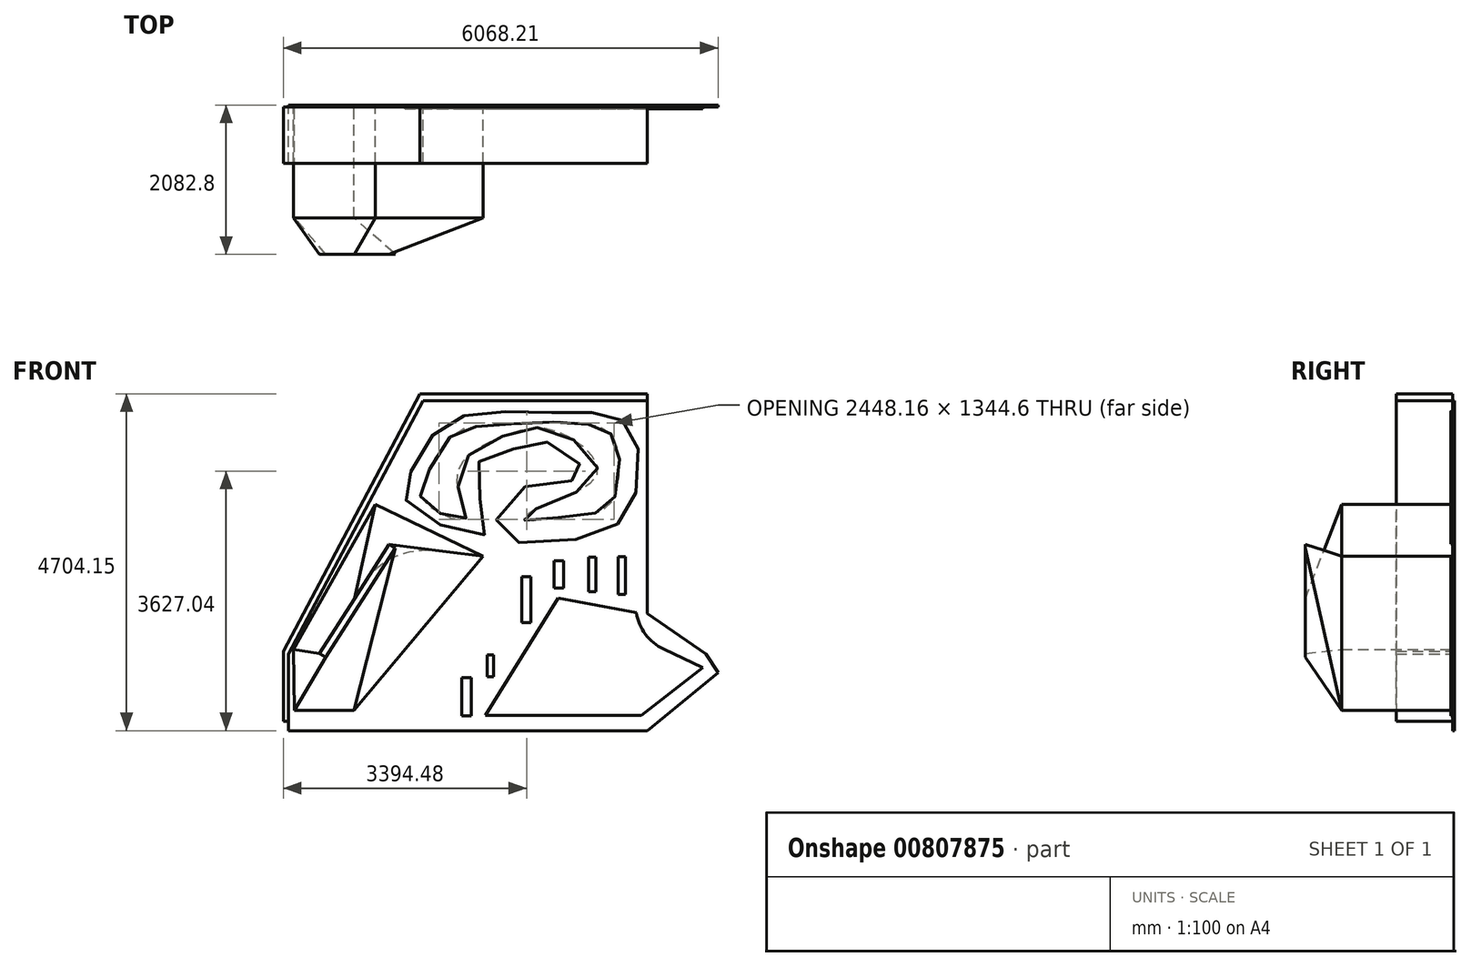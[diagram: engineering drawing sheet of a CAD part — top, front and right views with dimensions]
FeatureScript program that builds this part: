
annotation { "Feature Type Name" : "Feature", "Feature Type Description" : "" }
export const myFeature = defineFeature(function(context is Context, id is Id, definition is map)
    precondition{}
    {
        {
            var Q0;
            Q0=qCreatedBy(makeId("Front.planeOp"),FACE);
            var sketch = newSketch(context, id + "F0", { "sketchPlane" : qUnion([Q0])});
            skLineSegment(sketch, "E0.bottom", {"start": v(0, 0) * mm, "end": v(3810, 0) * mm});
            skLineSegment(sketch, "E0.top", {"start": v(1905, 4572) * mm, "end": v(3810, 4572) * mm});
            skLineSegment(sketch, "E0.left", {"start": v(0, 0) * mm, "end": v(0, 977.16) * mm});
            skLineSegment(sketch, "E1", {"start": v(1905, 4572) * mm, "end": v(0, 977.16) * mm});
            skPoint(sketch, "E2.orphan", {"position": v(0, 4572) * mm});
            skLineSegment(sketch, "E3", {"start": v(3810, 4572) * mm, "end": v(5080, 4572) * mm});
            skLineSegment(sketch, "E4", {"start": v(3810, 0) * mm, "end": v(5080, 0) * mm});
            skLineSegment(sketch, "E5", {"start": v(5080, 4572) * mm, "end": v(5080, 1518.6) * mm});
            skArc(sketch, "E6", {"start": v(5080, 1518.6) * mm, "mid": v(5146.41, 1287.08) * mm, "end": v(5325.45, 1125.96) * mm});
            skLineSegment(sketch, "E7", {"start": v(5325.45, 1125.96) * mm, "end": v(6071.5, 762.42) * mm});
            skLineSegment(sketch, "E8", {"start": v(6071.5, 762.42) * mm, "end": v(5080, 0) * mm});
            skPoint(sketch, "E9.end.orphan", {"position": v(3908.05, 0) * mm});
            skLineSegment(sketch, "E10", {"start": v(141.92, 1005.14) * mm, "end": v(153.82, 153.5) * mm});
            skLineSegment(sketch, "E11", {"start": v(153.82, 153.5) * mm, "end": v(985.88, 153.09) * mm});
            skLineSegment(sketch, "E12", {"start": v(985.88, 153.09) * mm, "end": v(2786.7, 2305.94) * mm});
            skLineSegment(sketch, "E13", {"start": v(2786.7, 2305.94) * mm, "end": v(1283.18, 3028.72) * mm});
            skLineSegment(sketch, "E14", {"start": v(1283.18, 3028.72) * mm, "end": v(141.92, 1005.14) * mm});
            skLineSegment(sketch, "E15", {"start": v(0, 977.16) * mm, "end": v(71.79, 939.12) * mm});
            skLineSegment(sketch, "E16", {"start": v(71.79, 939.12) * mm, "end": v(71.79, 0) * mm});
            skLineSegment(sketch, "E17", {"start": v(71.79, 0) * mm, "end": v(71.79, 939.12) * mm});
            skLineSegment(sketch, "E18", {"start": v(71.79, 939.12) * mm, "end": v(1996.95, 4572) * mm});
            skLineSegment(sketch, "E19", {"start": v(1905, 4572) * mm, "end": v(1947.78, 4479.21) * mm});
            skLineSegment(sketch, "E20", {"start": v(1947.78, 4479.21) * mm, "end": v(5080, 4479.21) * mm});
            skFitSpline(sketch, "E21", {"points": [v(1708.58, 3275.36) * mm, v(2109.58, 4028.05) * mm, v(2793.87, 4311.58) * mm, v(3872.47, 4311.04) * mm, v(4575.1, 4273.65) * mm, v(4920.08, 3946.4) * mm, v(4864.14, 3020.75) * mm, v(4296.89, 2589.05) * mm, v(3008.74, 2626.73) * mm, v(3372.71, 3274.52) * mm, v(4192.53, 3422.22) * mm, v(3779.8, 3872.93) * mm, v(3163.41, 3786.84) * mm, v(2657.86, 3490.87) * mm, v(2830, 2626.82) * mm, v(1825.53, 2960.57) * mm, v(1708.58, 3275.36) * mm]});
            skLineSegment(sketch, "E22", {"start": v(3372.71, 3274.52) * mm, "end": v(3526.64, 2965.88) * mm});
            skFitSpline(sketch, "E23", {"points": [v(3526.64, 2965.88) * mm, v(3347.83, 2817.87) * mm, v(4099.8, 2879.2) * mm, v(4586.8, 3045.58) * mm, v(4667.32, 3823.1) * mm, v(4476.38, 4082.4) * mm, v(3866.25, 4181.44) * mm, v(2830.76, 4126.42) * mm, v(2331.44, 3972.4) * mm, v(1930.45, 3244.4) * mm, v(1973.5, 3046.9) * mm, v(2528.09, 2812.1) * mm, v(2423.62, 3429.28) * mm, v(3027.9, 3965.87) * mm, v(3816.87, 4051.87) * mm, v(4383.61, 3459.15) * mm, v(3526.64, 2965.88) * mm]});
            skSolve(sketch);
        }
        {
            var Q0;
            {var subQ0=sQuery(id+"F0.wireOp",EDGE,"E4");Q0=makeQuery(id+"F0.imprint","IMPRINT",FACE,{"disambiguationData":[TD([[makeQuery(id+"F0.imprint","IMPRINT",EDGE,{"derivedFrom":subQ0}),1.0]])]});}
            var sketch = newSketch(context, id + "F1", { "sketchPlane" : qUnion([Q0])});
            skLineSegment(sketch, "E24", {"start": v(3837.36, 1720) * mm, "end": v(2819.86, 84.35) * mm});
            skLineSegment(sketch, "E25", {"start": v(2819.86, 84.35) * mm, "end": v(4997.1, 84.35) * mm});
            skLineSegment(sketch, "E26", {"start": v(4997.1, 84.35) * mm, "end": v(5855.95, 751.74) * mm});
            skLineSegment(sketch, "E27", {"start": v(5855.95, 751.74) * mm, "end": v(5308.9, 1008.85) * mm});
            skArc(sketch, "E28", {"start": v(4925.97, 1517.6) * mm, "mid": v(5054.35, 1215.74) * mm, "end": v(5308.9, 1008.85) * mm});
            skLineSegment(sketch, "E29", {"start": v(4925.97, 1517.6) * mm, "end": v(3837.36, 1720) * mm});
            skLineSegment(sketch, "E30.bottom", {"start": v(1605.43, 494.63) * mm, "end": v(1485.08, 494.63) * mm});
            skLineSegment(sketch, "E30.top", {"start": v(1605.43, 95.3) * mm, "end": v(1485.08, 95.3) * mm});
            skLineSegment(sketch, "E30.left", {"start": v(1605.43, 494.63) * mm, "end": v(1605.43, 95.3) * mm});
            skLineSegment(sketch, "E30.right", {"start": v(1485.08, 494.63) * mm, "end": v(1485.08, 95.3) * mm});
            skLineSegment(sketch, "E31.bottom", {"start": v(1846.13, 921.32) * mm, "end": v(1906.3, 921.32) * mm});
            skLineSegment(sketch, "E31.top", {"start": v(1846.13, 560.28) * mm, "end": v(1906.3, 560.28) * mm});
            skLineSegment(sketch, "E31.left", {"start": v(1846.13, 921.32) * mm, "end": v(1846.13, 560.28) * mm});
            skLineSegment(sketch, "E31.right", {"start": v(1906.3, 921.32) * mm, "end": v(1906.3, 560.28) * mm});
            skLineSegment(sketch, "E32.bottom", {"start": v(2907.4, 2037.29) * mm, "end": v(2989.45, 2037.29) * mm});
            skLineSegment(sketch, "E32.top", {"start": v(2907.4, 1659.83) * mm, "end": v(2989.45, 1659.83) * mm});
            skLineSegment(sketch, "E32.left", {"start": v(2907.4, 2037.29) * mm, "end": v(2907.4, 1659.83) * mm});
            skLineSegment(sketch, "E32.right", {"start": v(2989.45, 2037.29) * mm, "end": v(2989.45, 1659.83) * mm});
            skLineSegment(sketch, "E33.bottom", {"start": v(4674.34, 2299.87) * mm, "end": v(4778.27, 2299.87) * mm});
            skLineSegment(sketch, "E33.top", {"start": v(4674.34, 1769.24) * mm, "end": v(4778.27, 1769.24) * mm});
            skLineSegment(sketch, "E33.left", {"start": v(4674.34, 2299.87) * mm, "end": v(4674.34, 1769.24) * mm});
            skLineSegment(sketch, "E33.right", {"start": v(4778.27, 2299.87) * mm, "end": v(4778.27, 1769.24) * mm});
            skLineSegment(sketch, "E34.bottom", {"start": v(3328.61, 2020.88) * mm, "end": v(3454.43, 2020.88) * mm});
            skLineSegment(sketch, "E34.top", {"start": v(3328.61, 1375.37) * mm, "end": v(3454.43, 1375.37) * mm});
            skLineSegment(sketch, "E34.left", {"start": v(3328.61, 2020.88) * mm, "end": v(3328.61, 1375.37) * mm});
            skLineSegment(sketch, "E34.right", {"start": v(3454.43, 2020.88) * mm, "end": v(3454.43, 1375.37) * mm});
            skLineSegment(sketch, "E35.bottom", {"start": v(2486.17, 609.51) * mm, "end": v(2622.93, 609.51) * mm});
            skLineSegment(sketch, "E35.top", {"start": v(2486.17, 73.4) * mm, "end": v(2622.93, 73.4) * mm});
            skLineSegment(sketch, "E35.left", {"start": v(2486.17, 609.51) * mm, "end": v(2486.17, 73.4) * mm});
            skLineSegment(sketch, "E35.right", {"start": v(2622.93, 609.51) * mm, "end": v(2622.93, 73.4) * mm});
            skLineSegment(sketch, "E36.bottom", {"start": v(2847.22, 926.8) * mm, "end": v(2934.74, 926.8) * mm});
            skLineSegment(sketch, "E36.top", {"start": v(2847.22, 620.45) * mm, "end": v(2934.74, 620.45) * mm});
            skLineSegment(sketch, "E36.left", {"start": v(2847.22, 926.8) * mm, "end": v(2847.22, 620.45) * mm});
            skLineSegment(sketch, "E36.right", {"start": v(2934.74, 926.8) * mm, "end": v(2934.74, 620.45) * mm});
            skLineSegment(sketch, "E37.bottom", {"start": v(4264.05, 2294.4) * mm, "end": v(4362.52, 2294.4) * mm});
            skLineSegment(sketch, "E37.top", {"start": v(4264.05, 1813) * mm, "end": v(4362.52, 1813) * mm});
            skLineSegment(sketch, "E37.left", {"start": v(4264.05, 2294.4) * mm, "end": v(4264.05, 1813) * mm});
            skLineSegment(sketch, "E37.right", {"start": v(4362.52, 2294.4) * mm, "end": v(4362.52, 1813) * mm});
            skLineSegment(sketch, "E38.bottom", {"start": v(3777.19, 2239.7) * mm, "end": v(3913.95, 2239.7) * mm});
            skLineSegment(sketch, "E38.top", {"start": v(3777.19, 1862.24) * mm, "end": v(3913.95, 1862.24) * mm});
            skLineSegment(sketch, "E38.left", {"start": v(3777.19, 2239.7) * mm, "end": v(3777.19, 1862.24) * mm});
            skLineSegment(sketch, "E38.right", {"start": v(3913.95, 2239.7) * mm, "end": v(3913.95, 1862.24) * mm});
            skLineSegment(sketch, "E39.bottom", {"start": v(2201.7, 697.04) * mm, "end": v(2141.53, 697.04) * mm});
            skLineSegment(sketch, "E39.top", {"start": v(2201.7, 259.4) * mm, "end": v(2141.53, 259.4) * mm});
            skLineSegment(sketch, "E39.left", {"start": v(2201.7, 697.04) * mm, "end": v(2201.7, 259.4) * mm});
            skLineSegment(sketch, "E39.right", {"start": v(2141.53, 697.04) * mm, "end": v(2141.53, 259.4) * mm});
            skLineSegment(sketch, "E40", {"start": v(2070.42, 1462.9) * mm, "end": v(3273.2, 813.1) * mm});
            skLineSegment(sketch, "E41", {"start": v(2163.41, 1555.9) * mm, "end": v(3328.61, 902.18) * mm});
            skLineSegment(sketch, "E42", {"start": v(3328.61, 902.18) * mm, "end": v(2163.41, 1555.9) * mm});
            skLineSegment(sketch, "E43", {"start": v(2070.42, 1462.9) * mm, "end": v(2163.41, 1555.9) * mm});
            skSolve(sketch);
        }
        {
            var Q0;
            Q0=makeQuery(id+"F0.imprint","IMPRINT",FACE,{"disambiguationData":[TD([[makeQuery(id+"F0.imprint","IMPRINT",EDGE,{"derivedFrom":sQuery(id+"F0.wireOp",EDGE,"E21")}),-1.0]])]});
            var Q1;
            Q1=makeQuery(id+"F0.imprint","IMPRINT",FACE,{"disambiguationData":[TD([[makeQuery(id+"F0.imprint","IMPRINT",EDGE,{"derivedFrom":sQuery(id+"F0.wireOp",EDGE,"E10")}),1.0]])]});
            var Q2;
            {var subQ0=sQuery(id+"F1.wireOp",EDGE,"E25");Q2=makeQuery(id+"F1.imprint","IMPRINT",FACE,{"disambiguationData":[TD([[makeQuery(id+"F1.imprint","IMPRINT",EDGE,{"derivedFrom":subQ0}),1.0]])]});}
            var Q3;
            Q3=makeQuery(id+"F0.imprint","IMPRINT",FACE,{"disambiguationData":[TD([[makeQuery(id+"F0.imprint","IMPRINT",EDGE,{"derivedFrom":sQuery(id+"F0.wireOp",EDGE,"E1")}),1.0]])]});
            var Q4;
            {var subQ0=sQuery(id+"F0.wireOp",EDGE,"E19");Q4=makeQuery(id+"F0.imprint","IMPRINT",FACE,{"disambiguationData":[TD([[makeQuery(id+"F0.imprint","IMPRINT",EDGE,{"derivedFrom":subQ0}),1.0]])]});}
            var Q5;
            {var subQ4=sQuery(id+"F0.wireOp",EDGE,"E3");Q5=makeQuery(id+"F0.imprint","IMPRINT",FACE,{"disambiguationData":[TD([[makeQuery(id+"F0.imprint","IMPRINT",EDGE,{"derivedFrom":subQ4}),-1.0]])]});}
            var Q6;
            {var subQ0=sQuery(id+"F0.wireOp",EDGE,"E0.left");Q6=makeQuery(id+"F0.imprint","IMPRINT",FACE,{"disambiguationData":[TD([[makeQuery(id+"F0.imprint","IMPRINT",EDGE,{"derivedFrom":subQ0}),-1.0]])]});}
            var Q7;
            Q7=makeQuery(id+"F1.imprint","IMPRINT",FACE,{"disambiguationData":[TD([[makeQuery(id+"F1.imprint","IMPRINT",EDGE,{"derivedFrom":sQuery(id+"F1.wireOp",EDGE,"E35.bottom")}),-1.0]])]});
            var Q8;
            Q8=makeQuery(id+"F1.imprint","IMPRINT",FACE,{"disambiguationData":[TD([[makeQuery(id+"F1.imprint","IMPRINT",EDGE,{"derivedFrom":sQuery(id+"F1.wireOp",EDGE,"E36.bottom")}),-1.0]])]});
            var Q9;
            Q9=makeQuery(id+"F1.imprint","IMPRINT",FACE,{"disambiguationData":[TD([[makeQuery(id+"F1.imprint","IMPRINT",EDGE,{"derivedFrom":sQuery(id+"F1.wireOp",EDGE,"E34.bottom")}),-1.0]])]});
            var Q10;
            Q10=makeQuery(id+"F1.imprint","IMPRINT",FACE,{"disambiguationData":[TD([[makeQuery(id+"F1.imprint","IMPRINT",EDGE,{"derivedFrom":sQuery(id+"F1.wireOp",EDGE,"E38.bottom")}),-1.0]])]});
            var Q11;
            Q11=makeQuery(id+"F1.imprint","IMPRINT",FACE,{"disambiguationData":[TD([[makeQuery(id+"F1.imprint","IMPRINT",EDGE,{"derivedFrom":sQuery(id+"F1.wireOp",EDGE,"E37.bottom")}),-1.0]])]});
            var Q12;
            Q12=makeQuery(id+"F1.imprint","IMPRINT",FACE,{"disambiguationData":[TD([[makeQuery(id+"F1.imprint","IMPRINT",EDGE,{"derivedFrom":sQuery(id+"F1.wireOp",EDGE,"E33.bottom")}),-1.0]])]});
            extrude(context, id + "F2", {"entities" : qUnion([Q0, Q1, Q2, Q3, Q4, Q5, Q6, Q7, Q8, Q9, Q10, Q11, Q12]), "depth" : 25.4 * mm, "offsetDistance" : 25.4 * mm});
        }
        {
            var Q0;
            Q0=makeQuery(id+"F2.opExtrude","CAP_FACE",FACE,{"disambiguationData":[OSD([sQuery(id+"F0.wireOp",EDGE,"E10"),sQuery(id+"F0.wireOp",EDGE,"E11"),sQuery(id+"F0.wireOp",EDGE,"E12"),sQuery(id+"F0.wireOp",EDGE,"E13"),sQuery(id+"F0.wireOp",EDGE,"E14")])],"isStart":false});
            var sketch = newSketch(context, id + "F3", { "sketchPlane" : qUnion([Q0])});
            skSolve(sketch);
        }
        {
            var Q0;
            Q0=makeQuery(id+"F3.imprint","IMPRINT",FACE,{"disambiguationData":[TD([[makeQuery(id+"F3.imprint","IMPRINT",EDGE,{"derivedFrom":makeQuery(id+"F2.opExtrude","CAP_EDGE",EDGE,{"disambiguationData":[OSD([sQuery(id+"F0.wireOp",EDGE,"E10")])],"isStart":false})}),1.0]])]});
            extrude(context, id + "F4", {"entities" : qUnion([Q0]), "operationType" : NewBodyOperationType.ADD, "depth" : 1524 * mm, "offsetDistance" : 25.4 * mm});
        }
        {
            var Q0;
            Q0=makeQuery(id+"F4.opExtrude","CAP_FACE",FACE,{"disambiguationData":[OSD([sQuery(id+"F0.wireOp",EDGE,"E10"),sQuery(id+"F0.wireOp",EDGE,"E11"),sQuery(id+"F0.wireOp",EDGE,"E12"),sQuery(id+"F0.wireOp",EDGE,"E13"),sQuery(id+"F0.wireOp",EDGE,"E14")])],"isStart":false});
            cPlane(context, id + "F5", {"entities" : qUnion([Q0]), "cplaneType" : CPlaneType.OFFSET, "offset" : 508 * mm, "width" : 152.4 * mm, "height" : 152.4 * mm});
        }
        {
            var Q0;
            Q0=qCreatedBy(id+"F5.planeOp",FACE);
            var sketch = newSketch(context, id + "F6", { "sketchPlane" : qUnion([Q0])});
            skLineSegment(sketch, "E44", {"start": v(503.02, 944.77) * mm, "end": v(1474.87, 2472.2) * mm});
            skLineSegment(sketch, "E45", {"start": v(1474.87, 2472.2) * mm, "end": v(1560.92, 2417.45) * mm});
            skLineSegment(sketch, "E46", {"start": v(1560.92, 2417.45) * mm, "end": v(593.25, 896.58) * mm});
            skLineSegment(sketch, "E47", {"start": v(593.25, 896.58) * mm, "end": v(503.02, 944.77) * mm});
            skSolve(sketch);
        }
        {
            var Q1;
            Q1=makeQuery(id+"F6.imprint","IMPRINT",FACE,{"disambiguationData":[TD([[makeQuery(id+"F6.imprint","IMPRINT",EDGE,{"derivedFrom":sQuery(id+"F6.wireOp",EDGE,"E44")}),-1.0]])]});
            var Q2;
            Q2=makeQuery(id+"F4.opExtrude","CAP_FACE",FACE,{"disambiguationData":[OSD([sQuery(id+"F0.wireOp",EDGE,"E10"),sQuery(id+"F0.wireOp",EDGE,"E11"),sQuery(id+"F0.wireOp",EDGE,"E12"),sQuery(id+"F0.wireOp",EDGE,"E13"),sQuery(id+"F0.wireOp",EDGE,"E14")])],"isStart":false});
            loft(context, id + "F7", {"operationType" : NewBodyOperationType.ADD, "sheetProfilesArray" : [{ "sheetProfileEntities" : qUnion([Q1]) }, { "sheetProfileEntities" : qUnion([Q2]) }]});
        }
        {
            var Q0;
            Q0=makeQuery(id+"F2.opExtrude","CAP_FACE",FACE,{"disambiguationData":[OSD([sQuery(id+"F0.wireOp",EDGE,"E0.bottom"),sQuery(id+"F0.wireOp",EDGE,"E0.top"),sQuery(id+"F0.wireOp",EDGE,"E0.left"),sQuery(id+"F0.wireOp",EDGE,"E1"),sQuery(id+"F0.wireOp",EDGE,"E3"),sQuery(id+"F0.wireOp",EDGE,"E5"),sQuery(id+"F0.wireOp",EDGE,"E17"),sQuery(id+"F0.wireOp",EDGE,"E18"),sQuery(id+"F0.wireOp",EDGE,"E20")])],"isStart":false});
            extrude(context, id + "F8", {"entities" : qUnion([Q0]), "operationType" : NewBodyOperationType.ADD, "depth" : 762 * mm, "offsetDistance" : 25.4 * mm});
        }
        {
            var Q0;
            {var subQ0=sQuery(id+"F0.wireOp",EDGE,"E5");Q0=makeQuery(id+"F8.boolean.opBoolean","MERGE",FACE,{"derivedFrom":[makeQuery(id+"F2.opExtrude","SWEPT_FACE",FACE,{"disambiguationData":[OSD([subQ0])]}),makeQuery(id+"F8.opExtrude","SWEPT_FACE",FACE,{"disambiguationData":[OSD([subQ0])]})]});}
            var sketch = newSketch(context, id + "F9", { "sketchPlane" : qUnion([Q0])});
            skSolve(sketch);
        }
        {
            var Q0;
            Q0=makeQuery(id+"F2.opExtrude","CAP_FACE",FACE,{"disambiguationData":[OSD([sQuery(id+"F0.wireOp",EDGE,"E0.bottom"),sQuery(id+"F0.wireOp",EDGE,"E0.top"),sQuery(id+"F0.wireOp",EDGE,"E0.left"),sQuery(id+"F0.wireOp",EDGE,"E1"),sQuery(id+"F0.wireOp",EDGE,"E3"),sQuery(id+"F0.wireOp",EDGE,"E5"),sQuery(id+"F0.wireOp",EDGE,"E17"),sQuery(id+"F0.wireOp",EDGE,"E18"),sQuery(id+"F0.wireOp",EDGE,"E20")])],"isStart":true});
            var sketch = newSketch(context, id + "F10", { "sketchPlane" : qUnion([Q0])});
            skLineSegment(sketch, "E48", {"start": v(-5080, 4479.21) * mm, "end": v(-5080, 1503.27) * mm});
            skLineSegment(sketch, "E49", {"start": v(-5080, 1503.27) * mm, "end": v(-5899.33, 939.12) * mm});
            skLineSegment(sketch, "E50", {"start": v(-5899.33, 939.12) * mm, "end": v(-6068.2, 676.67) * mm});
            skLineSegment(sketch, "E51", {"start": v(-6068.2, 676.67) * mm, "end": v(-5080, -132.15) * mm});
            skLineSegment(sketch, "E52", {"start": v(-5080, -132.15) * mm, "end": v(-71.79, -132.15) * mm});
            skLineSegment(sketch, "E53", {"start": v(-71.79, -132.15) * mm, "end": v(-71.79, 0) * mm});
            skSolve(sketch);
        }
        {
            var Q0;
            Q0=makeQuery(id+"F10.imprint","IMPRINT",FACE,{"disambiguationData":[TD([[makeQuery(id+"F10.imprint","IMPRINT",EDGE,{"derivedFrom":sQuery(id+"F10.wireOp",EDGE,"E48")}),1.0]])]});
            extrude(context, id + "F11", {"entities" : qUnion([Q0]), "depth" : 25.4 * mm, "offsetDistance" : 25.4 * mm});
        }
    });
